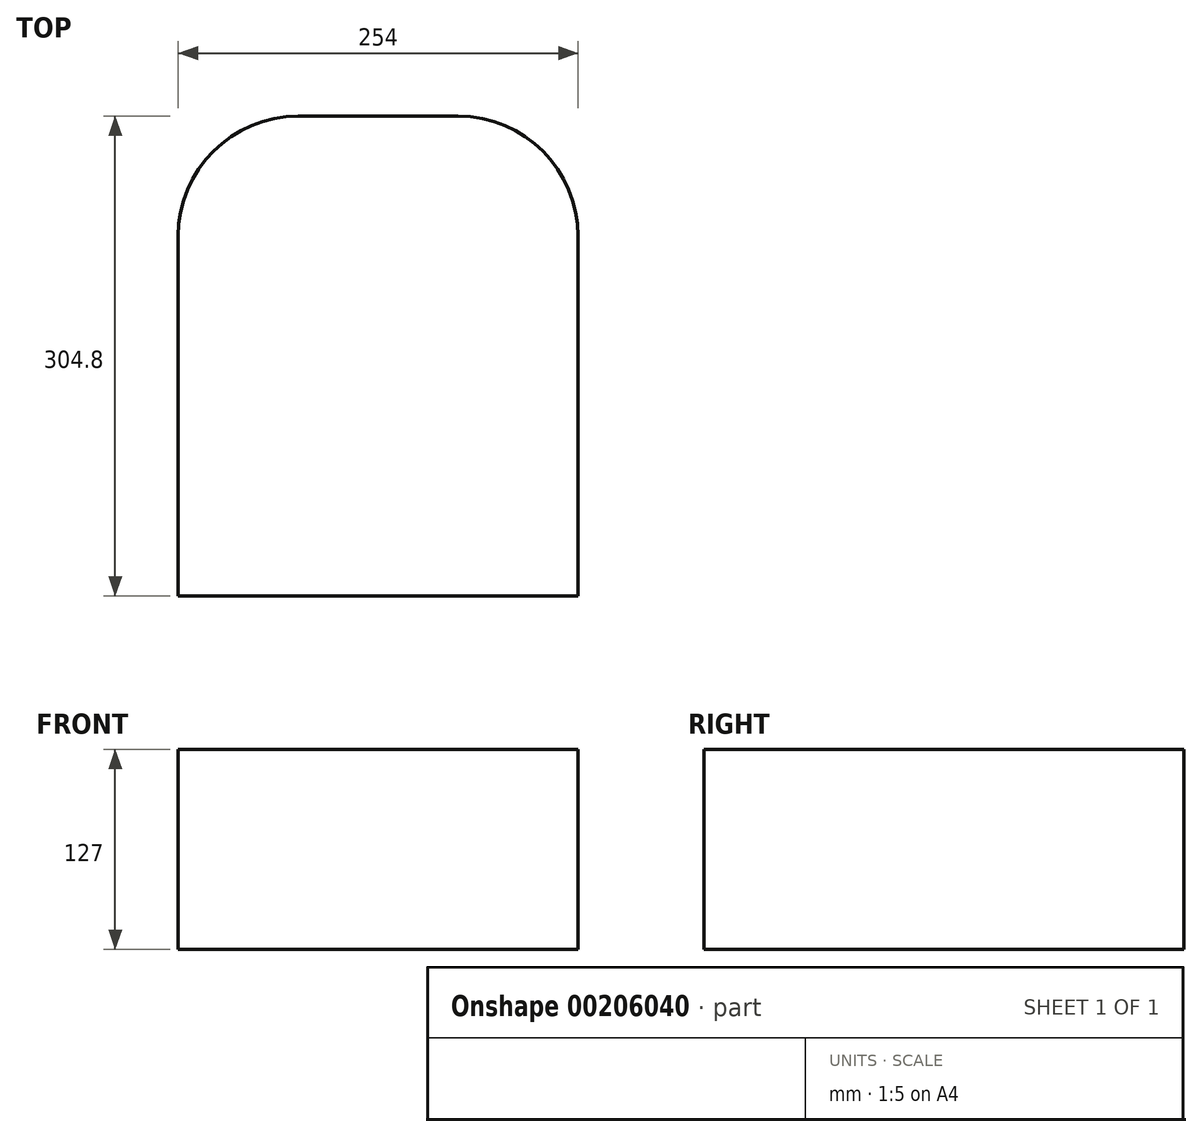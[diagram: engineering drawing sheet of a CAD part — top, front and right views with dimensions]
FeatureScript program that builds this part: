
annotation { "Feature Type Name" : "Feature", "Feature Type Description" : "" }
export const myFeature = defineFeature(function(context is Context, id is Id, definition is map)
    precondition{}
    {
        {
            var Q0;
            Q0=qCreatedBy(makeId("Front.planeOp"),FACE);
            var sketch = newSketch(context, id + "F0", { "sketchPlane" : qUnion([Q0])});
            skLineSegment(sketch, "E0.bottom", {"start": v(-127, 63.5) * mm, "end": v(127, 63.5) * mm});
            skLineSegment(sketch, "E0.top", {"start": v(-127, -63.5) * mm, "end": v(127, -63.5) * mm});
            skLineSegment(sketch, "E0.left", {"start": v(-127, 63.5) * mm, "end": v(-127, -63.5) * mm});
            skLineSegment(sketch, "E0.right", {"start": v(127, 63.5) * mm, "end": v(127, -63.5) * mm});
            skPoint(sketch, "E0.middle", {"position": v(0, 0) * mm});
            skSolve(sketch);
        }
        {
            var Q0;
            Q0=makeQuery(id+"F0.imprint","IMPRINT",FACE,{"disambiguationData":[TD([[makeQuery(id+"F0.imprint","IMPRINT",EDGE,{"derivedFrom":sQuery(id+"F0.wireOp",EDGE,"E0.bottom")}),-1.0]])]});
            extrude(context, id + "F1", {"entities" : qUnion([Q0]), "depth" : 304.8 * mm});
        }
        {
            var Q0;
            Q0=makeQuery(id+"F1.opExtrude","CAP_EDGE",EDGE,{"disambiguationData":[OSD([sQuery(id+"F0.wireOp",EDGE,"E0.left")])],"isStart":true});
            var Q1;
            Q1=makeQuery(id+"F1.opExtrude","CAP_EDGE",EDGE,{"disambiguationData":[OSD([sQuery(id+"F0.wireOp",EDGE,"E0.right")])],"isStart":true});
            fillet(context, id + "F2", {"entities" : qUnion([Q0, Q1]), "radius" : 76.2 * mm, "tangentPropagation" : true, "allowEdgeOverflow" : false});
        }
    });
